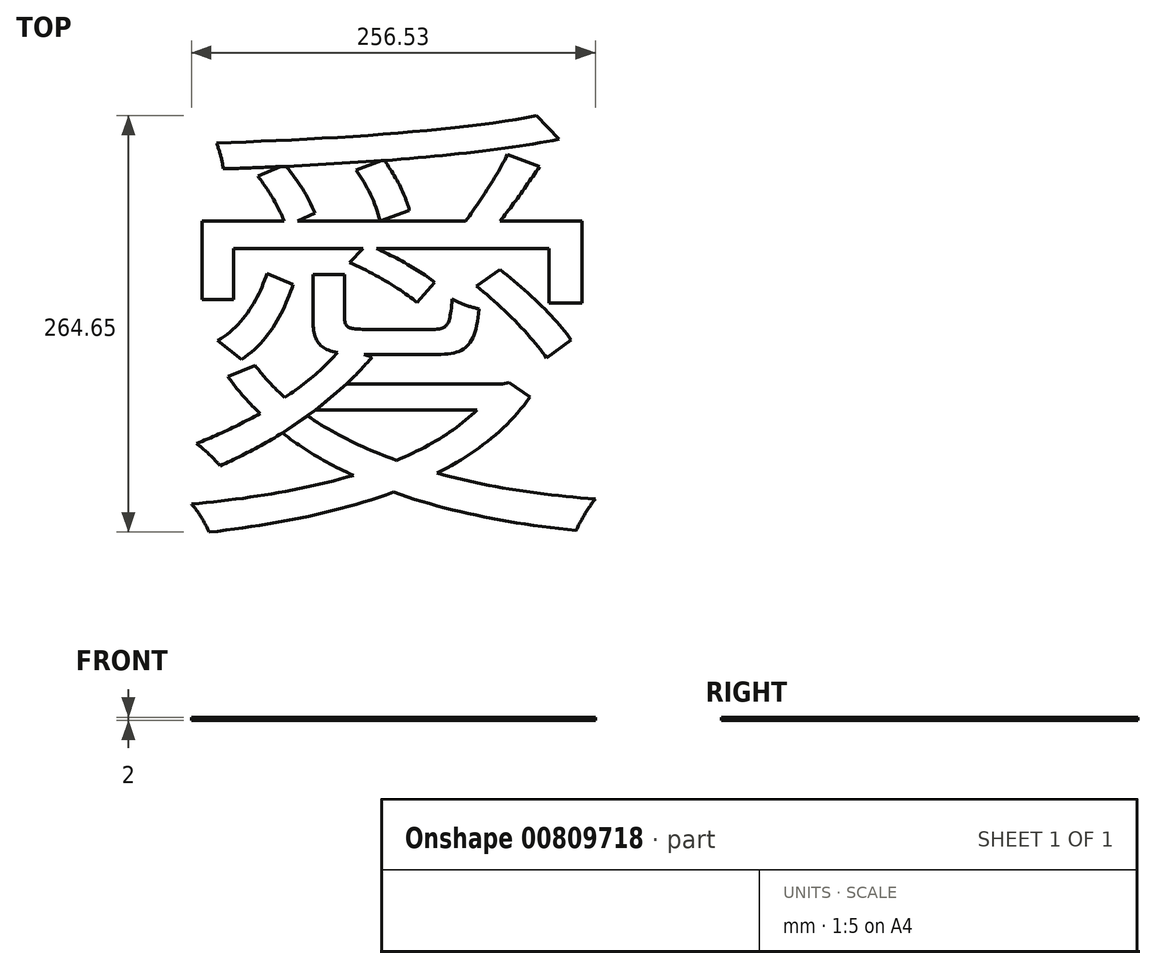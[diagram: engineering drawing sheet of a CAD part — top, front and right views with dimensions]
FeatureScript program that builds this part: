
annotation { "Feature Type Name" : "Feature", "Feature Type Description" : "" }
export const myFeature = defineFeature(function(context is Context, id is Id, definition is map)
    precondition{}
    {
        {
            var Q0;
            Q0=qCreatedBy(makeId("Top.planeOp"),FACE);
            var sketch = newSketch(context, id + "F0", { "sketchPlane" : qUnion([Q0])});
            skText(sketch, "E0", { "text": "愛", "fontName": "NotoSansCJKtc-Regular.otf"});
            const initialGuessF0  = {"E0": [0, 0, 1, 0, 0.208]};
            skSetInitialGuess(sketch, initialGuessF0);
            skSolve(sketch);
        }
        {
            var Q0;
            Q0=makeQuery(id+"F0.imprint","IMPRINT",FACE,{"disambiguationData":[TD([[makeQuery(id+"F0.imprint","IMPRINT",EDGE,{"derivedFrom":sQuery(id+"F0.wireOp",EDGE,"E0.sketch_text.stroke-32")}),1.0]])]});
            var Q1;
            Q1=makeQuery(id+"F0.imprint","IMPRINT",FACE,{"disambiguationData":[TD([[makeQuery(id+"F0.imprint","IMPRINT",EDGE,{"derivedFrom":sQuery(id+"F0.wireOp",EDGE,"E0.sketch_text.stroke-36")}),1.0]])]});
            var Q2;
            Q2=makeQuery(id+"F0.imprint","IMPRINT",FACE,{"disambiguationData":[TD([[makeQuery(id+"F0.imprint","IMPRINT",EDGE,{"derivedFrom":sQuery(id+"F0.wireOp",EDGE,"E0.sketch_text.stroke-0")}),1.0]])]});
            var Q3;
            Q3=makeQuery(id+"F0.imprint","IMPRINT",FACE,{"disambiguationData":[TD([[makeQuery(id+"F0.imprint","IMPRINT",EDGE,{"derivedFrom":sQuery(id+"F0.wireOp",EDGE,"E0.sketch_text.stroke-40")}),1.0]])]});
            var Q4;
            {var subQ1=sQuery(id+"F0.wireOp",EDGE,"E0.sketch_text.stroke-15");Q4=makeQuery(id+"F0.imprint","IMPRINT",FACE,{"disambiguationData":[TD([[makeQuery(id+"F0.imprint","IMPRINT",EDGE,{"derivedFrom":subQ1}),1.0]])]});}
            var Q5;
            {var subQ0=sQuery(id+"F0.wireOp",EDGE,"E0.sketch_text.stroke-14");Q5=makeQuery(id+"F0.imprint","IMPRINT",FACE,{"disambiguationData":[TD([[makeQuery(id+"F0.imprint","IMPRINT",EDGE,{"derivedFrom":subQ0}),-1.0]])]});}
            extrude(context, id + "F1", {"entities" : qUnion([Q0, Q1, Q2, Q3, Q4, Q5]), "depth" : 2 * mm, "offsetDistance" : 25.4 * mm});
        }
        {
            var Q0;
            Q0=qCreatedBy(makeId("Top.planeOp"),FACE);
            var sketch = newSketch(context, id + "F2", { "sketchPlane" : qUnion([Q0])});
            skLineSegment(sketch, "E1", {"start": v(84.42, 174.88) * mm, "end": v(136.73, 174.88) * mm});
            skArc(sketch, "E2", {"start": v(136.73, 174.88) * mm, "mid": v(130.76, 191.74) * mm, "end": v(121.55, 207.07) * mm});
            skLineSegment(sketch, "E3", {"start": v(121.55, 207.07) * mm, "end": v(138.18, 213.24) * mm});
            skLineSegment(sketch, "E4", {"start": v(138.18, 213.24) * mm, "end": v(77.08, 209.44) * mm});
            skArc(sketch, "E5", {"start": v(95.44, 179.77) * mm, "mid": v(87.53, 195.39) * mm, "end": v(77.08, 209.44) * mm});
            skLineSegment(sketch, "E6", {"start": v(95.44, 179.77) * mm, "end": v(84.42, 174.88) * mm});
            skSolve(sketch);
        }
        {
            var Q0;
            Q0 = qSketchRegion(id + "F2", true);
            extrude(context, id + "F3", {"entities" : qUnion([Q0]), "operationType" : NewBodyOperationType.REMOVE, "depth" : 25.4 * mm, "offsetDistance" : 25.4 * mm});
        }
        {
            var Q0;
            Q0=makeQuery(id+"F1.opExtrude","CAP_FACE",FACE,{"disambiguationData":[OSD([sQuery(id+"F0.wireOp",EDGE,"E0.sketch_text.stroke-0"),sQuery(id+"F0.wireOp",EDGE,"E0.sketch_text.stroke-1"),sQuery(id+"F0.wireOp",EDGE,"E0.sketch_text.stroke-2"),sQuery(id+"F0.wireOp",EDGE,"E0.sketch_text.stroke-3"),sQuery(id+"F0.wireOp",EDGE,"E0.sketch_text.stroke-4"),sQuery(id+"F0.wireOp",EDGE,"E0.sketch_text.stroke-5"),sQuery(id+"F0.wireOp",EDGE,"E0.sketch_text.stroke-6"),sQuery(id+"F0.wireOp",EDGE,"E0.sketch_text.stroke-7"),sQuery(id+"F0.wireOp",EDGE,"E0.sketch_text.stroke-8"),sQuery(id+"F0.wireOp",EDGE,"E0.sketch_text.stroke-9"),sQuery(id+"F0.wireOp",EDGE,"E0.sketch_text.stroke-10"),sQuery(id+"F0.wireOp",EDGE,"E0.sketch_text.stroke-11"),sQuery(id+"F0.wireOp",EDGE,"E0.sketch_text.stroke-12"),sQuery(id+"F0.wireOp",EDGE,"E0.sketch_text.stroke-13"),sQuery(id+"F0.wireOp",EDGE,"E0.sketch_text.stroke-19"),sQuery(id+"F0.wireOp",EDGE,"E0.sketch_text.stroke-20"),sQuery(id+"F0.wireOp",EDGE,"E0.sketch_text.stroke-21"),sQuery(id+"F0.wireOp",EDGE,"E0.sketch_text.stroke-22"),sQuery(id+"F0.wireOp",EDGE,"E0.sketch_text.stroke-23"),sQuery(id+"F0.wireOp",EDGE,"E0.sketch_text.stroke-24"),sQuery(id+"F0.wireOp",EDGE,"E0.sketch_text.stroke-25"),sQuery(id+"F0.wireOp",EDGE,"E0.sketch_text.stroke-26"),sQuery(id+"F0.wireOp",EDGE,"E0.sketch_text.stroke-27"),sQuery(id+"F0.wireOp",EDGE,"E0.sketch_text.stroke-28"),sQuery(id+"F0.wireOp",EDGE,"E0.sketch_text.stroke-29"),sQuery(id+"F0.wireOp",EDGE,"E0.sketch_text.stroke-30"),sQuery(id+"F0.wireOp",EDGE,"E0.sketch_text.stroke-31")])],"isStart":false});
            var sketch = newSketch(context, id + "F4", { "sketchPlane" : qUnion([Q0])});
            skLineSegment(sketch, "E7", {"start": v(73.94, 209.44) * mm, "end": v(77.08, 209.44) * mm});
            skLineSegment(sketch, "E8", {"start": v(138.18, 213.24) * mm, "end": v(139.52, 213.2) * mm});
            skLineSegment(sketch, "E9", {"start": v(73.94, 209.44) * mm, "end": v(73.7, 209.34) * mm});
            skLineSegment(sketch, "E10", {"start": v(73.7, 209.34) * mm, "end": v(77.17, 209.34) * mm});
            skLineSegment(sketch, "E11", {"start": v(77.17, 209.34) * mm, "end": v(77.08, 209.44) * mm});
            skLineSegment(sketch, "E12", {"start": v(138.18, 213.24) * mm, "end": v(137.93, 213.14) * mm});
            skLineSegment(sketch, "E13", {"start": v(137.93, 213.14) * mm, "end": v(139.6, 213.09) * mm});
            skLineSegment(sketch, "E14", {"start": v(139.6, 213.09) * mm, "end": v(139.52, 213.2) * mm});
            skSolve(sketch);
        }
        {
            var Q0;
            Q0 = qSketchRegion(id + "F4", true);
            extrude(context, id + "F5", {"entities" : qUnion([Q0]), "operationType" : NewBodyOperationType.REMOVE, "oppositeDirection" : true, "depth" : 25.4 * mm, "offsetDistance" : 25.4 * mm});
        }
        {
            var Q0;
            Q0=makeQuery(id+"F1.opExtrude","CAP_FACE",FACE,{"disambiguationData":[OSD([sQuery(id+"F0.wireOp",EDGE,"E0.sketch_text.stroke-40"),sQuery(id+"F0.wireOp",EDGE,"E0.sketch_text.stroke-41"),sQuery(id+"F0.wireOp",EDGE,"E0.sketch_text.stroke-42"),sQuery(id+"F0.wireOp",EDGE,"E0.sketch_text.stroke-43"),sQuery(id+"F0.wireOp",EDGE,"E0.sketch_text.stroke-44"),sQuery(id+"F0.wireOp",EDGE,"E0.sketch_text.stroke-45"),sQuery(id+"F0.wireOp",EDGE,"E0.sketch_text.stroke-46"),sQuery(id+"F0.wireOp",EDGE,"E0.sketch_text.stroke-47"),sQuery(id+"F0.wireOp",EDGE,"E0.sketch_text.stroke-48"),sQuery(id+"F0.wireOp",EDGE,"E0.sketch_text.stroke-49"),sQuery(id+"F0.wireOp",EDGE,"E0.sketch_text.stroke-50"),sQuery(id+"F0.wireOp",EDGE,"E0.sketch_text.stroke-51"),sQuery(id+"F0.wireOp",EDGE,"E0.sketch_text.stroke-52"),sQuery(id+"F0.wireOp",EDGE,"E0.sketch_text.stroke-53"),sQuery(id+"F0.wireOp",EDGE,"E0.sketch_text.stroke-54"),sQuery(id+"F0.wireOp",EDGE,"E0.sketch_text.stroke-55"),sQuery(id+"F0.wireOp",EDGE,"E0.sketch_text.stroke-56"),sQuery(id+"F0.wireOp",EDGE,"E0.sketch_text.stroke-57"),sQuery(id+"F0.wireOp",EDGE,"E0.sketch_text.stroke-58"),sQuery(id+"F0.wireOp",EDGE,"E0.sketch_text.stroke-59"),sQuery(id+"F0.wireOp",EDGE,"E0.sketch_text.stroke-60"),sQuery(id+"F0.wireOp",EDGE,"E0.sketch_text.stroke-61"),sQuery(id+"F0.wireOp",EDGE,"E0.sketch_text.stroke-62"),sQuery(id+"F0.wireOp",EDGE,"E0.sketch_text.stroke-63"),sQuery(id+"F0.wireOp",EDGE,"E0.sketch_text.stroke-64"),sQuery(id+"F0.wireOp",EDGE,"E0.sketch_text.stroke-65"),sQuery(id+"F0.wireOp",EDGE,"E0.sketch_text.stroke-66"),sQuery(id+"F0.wireOp",EDGE,"E0.sketch_text.stroke-67"),sQuery(id+"F0.wireOp",EDGE,"E0.sketch_text.stroke-68"),sQuery(id+"F0.wireOp",EDGE,"E0.sketch_text.stroke-69"),sQuery(id+"F0.wireOp",EDGE,"E0.sketch_text.stroke-70"),sQuery(id+"F0.wireOp",EDGE,"E0.sketch_text.stroke-71"),sQuery(id+"F0.wireOp",EDGE,"E0.sketch_text.stroke-72"),sQuery(id+"F0.wireOp",EDGE,"E0.sketch_text.stroke-73")])],"isStart":false});
            var sketch = newSketch(context, id + "F6", { "sketchPlane" : qUnion([Q0])});
            skLineSegment(sketch, "E15", {"start": v(95.92, 54.89) * mm, "end": v(115.56, 71.36) * mm});
            skLineSegment(sketch, "E16", {"start": v(115.56, 71.36) * mm, "end": v(115.71, 71.36) * mm});
            skLineSegment(sketch, "E17", {"start": v(115.71, 71.36) * mm, "end": v(96.08, 54.89) * mm});
            skLineSegment(sketch, "E18", {"start": v(96.08, 54.89) * mm, "end": v(95.92, 54.89) * mm});
            skLineSegment(sketch, "E19", {"start": v(90.73, 51.14) * mm, "end": v(74.84, 40.17) * mm});
            skLineSegment(sketch, "E20", {"start": v(74.84, 40.17) * mm, "end": v(74.92, 40.11) * mm});
            skLineSegment(sketch, "E21", {"start": v(74.92, 40.11) * mm, "end": v(90.81, 51.09) * mm});
            skLineSegment(sketch, "E22", {"start": v(90.81, 51.09) * mm, "end": v(90.73, 51.14) * mm});
            skSolve(sketch);
        }
        {
            var Q0;
            Q0 = qSketchRegion(id + "F6", true);
            extrude(context, id + "F7", {"entities" : qUnion([Q0]), "operationType" : NewBodyOperationType.REMOVE, "oppositeDirection" : true, "depth" : 25.4 * mm, "offsetDistance" : 25.4 * mm});
        }
    });
